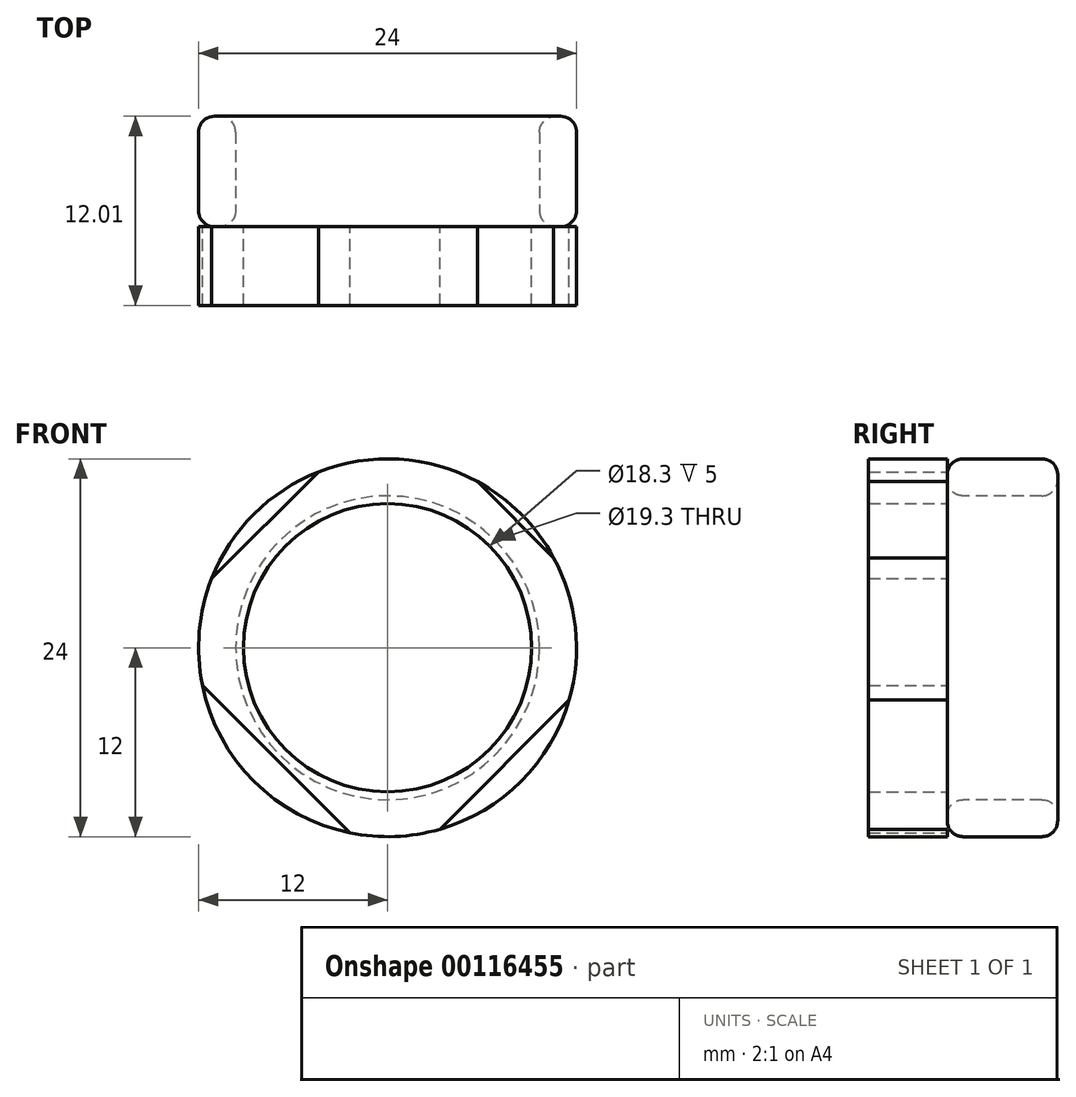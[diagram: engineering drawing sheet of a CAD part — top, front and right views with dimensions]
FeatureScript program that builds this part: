
annotation { "Feature Type Name" : "Feature", "Feature Type Description" : "" }
export const myFeature = defineFeature(function(context is Context, id is Id, definition is map)
    precondition{}
    {
        {
            var Q0;
            Q0=qCreatedBy(makeId("Front.planeOp"),FACE);
            var sketch = newSketch(context, id + "F0", { "sketchPlane" : qUnion([Q0])});
            skCircle(sketch, "E0", {"center": v(0, 0) * mm, "radius": 12 * mm});
            skCircle(sketch, "E1", {"center": v(0, 0) * mm, "radius": 9.65 * mm});
            skSolve(sketch);
        }
        {
            var Q0;
            Q0=makeQuery(id+"F0.imprint","IMPRINT",FACE,{"disambiguationData":[TD([[makeQuery(id+"F0.imprint","IMPRINT",EDGE,{"derivedFrom":sQuery(id+"F0.wireOp",EDGE,"E0")}),1.0]])]});
            extrude(context, id + "F1", {"entities" : qUnion([Q0]), "oppositeDirection" : true, "depth" : 7 * mm});
        }
        {
            var Q0;
            Q0=makeQuery(id+"F1.opExtrude","CAP_EDGE",EDGE,{"disambiguationData":[OSD([sQuery(id+"F0.wireOp",EDGE,"E0")])],"isStart":true});
            var Q1;
            Q1=makeQuery(id+"F1.opExtrude","CAP_EDGE",EDGE,{"disambiguationData":[OSD([sQuery(id+"F0.wireOp",EDGE,"E0")])],"isStart":false});
            var Q2;
            Q2=makeQuery(id+"F1.opExtrude","CAP_EDGE",EDGE,{"disambiguationData":[OSD([sQuery(id+"F0.wireOp",EDGE,"E1")])],"isStart":true});
            var Q3;
            Q3=makeQuery(id+"F1.opExtrude","CAP_EDGE",EDGE,{"disambiguationData":[OSD([sQuery(id+"F0.wireOp",EDGE,"E1")])],"isStart":false});
            fillet(context, id + "F2", {"entities" : qUnion([Q0, Q1, Q2, Q3]), "radius" : 1 * mm, "tangentPropagation" : true, "allowEdgeOverflow" : false});
        }
        {
            var Q0;
            Q0=makeQuery(id+"F0.imprint","IMPRINT",FACE,{"disambiguationData":[TD([[makeQuery(id+"F0.imprint","IMPRINT",EDGE,{"derivedFrom":sQuery(id+"F0.wireOp",EDGE,"E1")}),1.0]])]});
            var sketch = newSketch(context, id + "F3", { "sketchPlane" : qUnion([Q0])});
            skCircle(sketch, "E2.0", {"center": v(0, 0) * mm, "radius": 9.65 * mm, "construction": true});
            skCircle(sketch, "E3", {"center": v(0, 0) * mm, "radius": 9.15 * mm});
            skArc(sketch, "E4", {"start": v(-11.17, 4.39) * mm, "mid": v(-11.95, 1.05) * mm, "end": v(-11.76, -2.38) * mm});
            skLineSegment(sketch, "E5", {"start": v(-8.49, 8.49) * mm, "end": v(8.49, -8.49) * mm, "construction": true});
            skLineSegment(sketch, "E6", {"start": v(-8.49, -8.49) * mm, "end": v(8.49, 8.49) * mm, "construction": true});
            skLineSegment(sketch, "E7", {"start": v(0, 0) * mm, "end": v(0, 12) * mm, "construction": true});
            skLineSegment(sketch, "E8", {"start": v(-11.17, 4.39) * mm, "end": v(-4.39, 11.17) * mm});
            skLineSegment(sketch, "E9", {"start": v(5.7, 10.56) * mm, "end": v(10.56, 5.7) * mm});
            skLineSegment(sketch, "E10", {"start": v(3.32, -11.53) * mm, "end": v(11.53, -3.32) * mm});
            skLineSegment(sketch, "E11", {"start": v(-11.76, -2.38) * mm, "end": v(-2.38, -11.76) * mm});
            skArc(sketch, "E12.trimOffspring", {"start": v(-2.38, -11.76) * mm, "mid": v(0.48, -12) * mm, "end": v(3.32, -11.53) * mm});
            skArc(sketch, "E13.trimOffspring", {"start": v(11.53, -3.32) * mm, "mid": v(11.93, 1.3) * mm, "end": v(10.56, 5.7) * mm});
            skArc(sketch, "E14.trimOffspring", {"start": v(5.7, 10.56) * mm, "mid": v(0.73, 11.98) * mm, "end": v(-4.39, 11.17) * mm});
            skSolve(sketch);
        }
        {
            var Q0;
            Q0=makeQuery(id+"F3.imprint","IMPRINT",FACE,{"disambiguationData":[TD([[makeQuery(id+"F3.imprint","IMPRINT",EDGE,{"derivedFrom":sQuery(id+"F3.wireOp",EDGE,"E4")}),1.0]])]});
            var Q1;
            Q1=makeQuery(id+"F3.imprint","IMPRINT",FACE,{"disambiguationData":[TD([[makeQuery(id+"F3.imprint","IMPRINT",EDGE,{"derivedFrom":sQuery(id+"F3.wireOp",EDGE,"E3")}),-1.0]])]});
            extrude(context, id + "F4", {"entities" : qUnion([Q0, Q1]), "depth" : 5 * mm});
        }
    });
